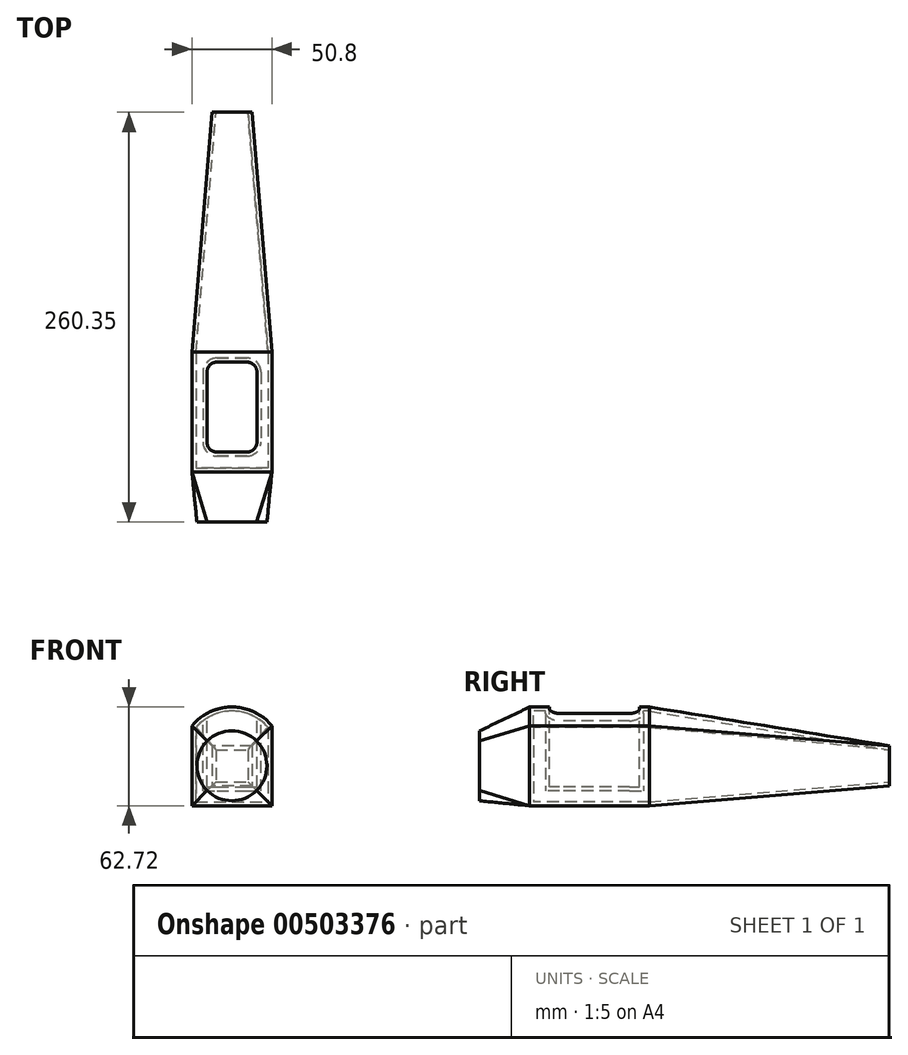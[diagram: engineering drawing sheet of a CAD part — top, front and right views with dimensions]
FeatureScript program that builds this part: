
annotation { "Feature Type Name" : "Feature", "Feature Type Description" : "" }
export const myFeature = defineFeature(function(context is Context, id is Id, definition is map)
    precondition{}
    {
        {
            var Q0;
            Q0=qCreatedBy(makeId("Front.planeOp"),FACE);
            var sketch = newSketch(context, id + "F0", { "sketchPlane" : qUnion([Q0])});
            skLineSegment(sketch, "E0.bottom", {"start": v(-25.4, 25.4) * mm, "end": v(25.4, 25.4) * mm});
            skLineSegment(sketch, "E0.top", {"start": v(-25.4, -25.4) * mm, "end": v(25.4, -25.4) * mm});
            skLineSegment(sketch, "E0.left", {"start": v(-25.4, 25.4) * mm, "end": v(-25.4, -25.4) * mm});
            skLineSegment(sketch, "E0.right", {"start": v(25.4, 25.4) * mm, "end": v(25.4, -25.4) * mm});
            skArc(sketch, "E1", {"start": v(25.4, 25.4) * mm, "mid": v(0, 37.32) * mm, "end": v(-25.4, 25.4) * mm});
            skSolve(sketch);
        }
        {
            var Q0;
            Q0=makeQuery(id+"F0.imprint","IMPRINT",FACE,{"disambiguationData":[TD([[makeQuery(id+"F0.imprint","IMPRINT",EDGE,{"derivedFrom":sQuery(id+"F0.wireOp",EDGE,"E0.bottom")}),-1.0]])]});
            var Q1;
            Q1=makeQuery(id+"F0.imprint","IMPRINT",FACE,{"disambiguationData":[TD([[makeQuery(id+"F0.imprint","IMPRINT",EDGE,{"derivedFrom":sQuery(id+"F0.wireOp",EDGE,"E0.bottom")}),1.0]])]});
            extrude(context, id + "F1", {"entities" : qUnion([Q0, Q1]), "oppositeDirection" : true, "depth" : 76.2 * mm});
        }
        {
            var Q0;
            Q0=makeQuery(id+"F1.opExtrude","CAP_FACE",FACE,{"disambiguationData":[OSD([sQuery(id+"F0.wireOp",EDGE,"E0.top"),sQuery(id+"F0.wireOp",EDGE,"E0.left"),sQuery(id+"F0.wireOp",EDGE,"E0.right"),sQuery(id+"F0.wireOp",EDGE,"E1")])],"isStart":false});
            cPlane(context, id + "F2", {"entities" : qUnion([Q0]), "cplaneType" : CPlaneType.OFFSET, "offset" : 152.4 * mm, "width" : 152.4 * mm, "height" : 152.4 * mm});
        }
        {
            var Q0;
            Q0=qCreatedBy(id+"F2.planeOp",FACE);
            var sketch = newSketch(context, id + "F3", { "sketchPlane" : qUnion([Q0])});
            skLineSegment(sketch, "E2.bottom", {"start": v(-12.7, 12.7) * mm, "end": v(12.7, 12.7) * mm});
            skLineSegment(sketch, "E2.top", {"start": v(-12.7, -12.7) * mm, "end": v(12.7, -12.7) * mm});
            skLineSegment(sketch, "E2.left", {"start": v(-12.7, 12.7) * mm, "end": v(-12.7, -12.7) * mm});
            skLineSegment(sketch, "E2.right", {"start": v(12.7, 12.7) * mm, "end": v(12.7, -12.7) * mm});
            skSolve(sketch);
        }
        {
            var Q1;
            Q1=makeQuery(id+"F1.opExtrude","CAP_FACE",FACE,{"disambiguationData":[OSD([sQuery(id+"F0.wireOp",EDGE,"E0.top"),sQuery(id+"F0.wireOp",EDGE,"E0.left"),sQuery(id+"F0.wireOp",EDGE,"E0.right"),sQuery(id+"F0.wireOp",EDGE,"E1")])],"isStart":false});
            var Q2;
            Q2=makeQuery(id+"F3.imprint","IMPRINT",FACE,{"disambiguationData":[TD([[makeQuery(id+"F3.imprint","IMPRINT",EDGE,{"derivedFrom":sQuery(id+"F3.wireOp",EDGE,"E2.bottom")}),-1.0]])]});
            loft(context, id + "F4", {"operationType" : NewBodyOperationType.ADD, "sheetProfilesArray" : [{ "sheetProfileEntities" : qUnion([Q1]) }, { "sheetProfileEntities" : qUnion([Q2]) }]});
        }
        {
            var Q0;
            Q0=makeQuery(id+"F1.opExtrude","CAP_EDGE",EDGE,{"disambiguationData":[OSD([sQuery(id+"F0.wireOp",EDGE,"E1")])],"isStart":true});
            cPoint(context, id + "F5", {"entities" : qUnion([Q0]), "parameter" : 0.5});
        }
        {
            var Q0;
            Q0 = qCreatedBy(id + "F5" ,VERTEX);
            var Q1;
            Q1=qCreatedBy(makeId("Top.planeOp"),FACE);
            cPlane(context, id + "F6", {"entities" : qUnion([Q0, Q1]), "cplaneType" : CPlaneType.PLANE_POINT, "offset" : 25.4 * mm, "width" : 152.4 * mm, "height" : 152.4 * mm});
        }
        {
            var Q0;
            Q0=qCreatedBy(id+"F6.planeOp",FACE);
            var sketch = newSketch(context, id + "F7", { "sketchPlane" : qUnion([Q0])});
            skLineSegment(sketch, "E3.bottom", {"start": v(-9.53, 69.85) * mm, "end": v(9.52, 69.85) * mm});
            skLineSegment(sketch, "E3.top", {"start": v(-9.53, 12.7) * mm, "end": v(9.52, 12.7) * mm});
            skLineSegment(sketch, "E3.left", {"start": v(-15.88, 63.5) * mm, "end": v(-15.88, 19.05) * mm});
            skLineSegment(sketch, "E3.right", {"start": v(15.87, 63.5) * mm, "end": v(15.87, 19.05) * mm});
            skPoint(sketch, "E4.visualSharp", {"position": v(-15.88, 69.85) * mm});
            skArc(sketch, "E4.filletArc", {"start": v(-9.53, 69.85) * mm, "mid": v(-14.02, 68) * mm, "end": v(-15.88, 63.5) * mm});
            skPoint(sketch, "E5.visualSharp", {"position": v(-15.88, 12.7) * mm});
            skArc(sketch, "E5.filletArc", {"start": v(-15.88, 19.05) * mm, "mid": v(-14.02, 14.56) * mm, "end": v(-9.53, 12.7) * mm});
            skPoint(sketch, "E6.visualSharp", {"position": v(15.87, 12.7) * mm});
            skArc(sketch, "E6.filletArc", {"start": v(9.52, 12.7) * mm, "mid": v(14.02, 14.56) * mm, "end": v(15.87, 19.05) * mm});
            skPoint(sketch, "E7.visualSharp", {"position": v(15.87, 69.85) * mm});
            skArc(sketch, "E7.filletArc", {"start": v(15.87, 63.5) * mm, "mid": v(14.02, 68) * mm, "end": v(9.52, 69.85) * mm});
            skSolve(sketch);
        }
        {
            var Q0;
            Q0=makeQuery(id+"F7.imprint","IMPRINT",FACE,{"disambiguationData":[TD([[makeQuery(id+"F7.imprint","IMPRINT",EDGE,{"derivedFrom":sQuery(id+"F7.wireOp",EDGE,"E3.bottom")}),-1.0]])]});
            extrude(context, id + "F8", {"entities" : qUnion([Q0]), "operationType" : NewBodyOperationType.REMOVE, "oppositeDirection" : true, "depth" : 50.8 * mm});
        }
        {
            var Q0;
            Q0=makeQuery(id+"F4.opLoft","CAP_FACE",FACE,{"disambiguationData":[OSD([makeQuery(id+"F3.imprint","IMPRINT",FACE,{"disambiguationData":[TD([[makeQuery(id+"F3.imprint","IMPRINT",EDGE,{"derivedFrom":sQuery(id+"F3.wireOp",EDGE,"E2.bottom")}),-1.0]])]})])],"isStart":true});
            shell(context, id + "F9", {"entities" : qUnion([Q0]), "thickness" : 2.54 * mm});
        }
        {
            var Q0;
            Q0=qCreatedBy(makeId("Front.planeOp"),FACE);
            cPlane(context, id + "F10", {"entities" : qUnion([Q0]), "cplaneType" : CPlaneType.OFFSET, "offset" : 31.75 * mm, "width" : 152.4 * mm, "height" : 152.4 * mm});
        }
        {
            var Q0;
            Q0=qCreatedBy(id+"F10.planeOp",FACE);
            var sketch = newSketch(context, id + "F11", { "sketchPlane" : qUnion([Q0])});
            skCircle(sketch, "E8", {"center": v(0, 0) * mm, "radius": 22.23 * mm});
            skSolve(sketch);
        }
        {
            var Q1;
            Q1=makeQuery(id+"F11.imprint","IMPRINT",FACE,{"disambiguationData":[TD([[makeQuery(id+"F11.imprint","IMPRINT",EDGE,{"derivedFrom":sQuery(id+"F11.wireOp",EDGE,"E8")}),1.0]])]});
            var Q2;
            Q2=makeQuery(id+"F1.opExtrude","CAP_FACE",FACE,{"disambiguationData":[OSD([sQuery(id+"F0.wireOp",EDGE,"E0.top"),sQuery(id+"F0.wireOp",EDGE,"E0.left"),sQuery(id+"F0.wireOp",EDGE,"E0.right"),sQuery(id+"F0.wireOp",EDGE,"E1")])],"isStart":true});
            loft(context, id + "F12", {"operationType" : NewBodyOperationType.ADD, "sheetProfilesArray" : [{ "sheetProfileEntities" : qUnion([Q1]) }, { "sheetProfileEntities" : qUnion([Q2]) }]});
        }
    });
